FCSTD DOCUMENT  (FreeCAD 0.19R24267 +99 (Git))
Label: OTP20_PCB_Assembly
License: Creative Commons Attribution-NonCommercial-ShareAlike
LicenseURL: http://creativecommons.org/licenses/by-nc-sa/4.0/
objects: App::Link×6, App::DocumentObjectGroup×2, PartDesign::CoordinateSystem×1, App::FeaturePython×1, App::Part×1
note: 1 computed .brp shape members not serialized (recipe doc carries the construction recipe); baked Part::Feature solids carry a one-line shape summary decoded from their .brp
EXTERNAL_REF file=PCB_Outline.FCStd obj=LCS_0
EXTERNAL_REF file=PCB_Outline.FCStd obj=PCB_Board
EXTERNAL_REF file=../20_COTS/Lightpipe_Mentor_1296-2012.FCStd obj=LCS_0
EXTERNAL_REF file=../20_COTS/Lightpipe_Mentor_1296-2012.FCStd obj=Lightpipe
EXTERNAL_REF file=../20_COTS/USB_A_Connector_Wuerth.FCStd obj=USB_A_Connector
EXTERNAL_REF file=../20_COTS/USB_A_Connector_Wuerth.FCStd obj=LCS_0
EXTERNAL_REF file=../20_COTS/USB_C_Connector_Wuerth.FCStd obj=USB_C_Connector
EXTERNAL_REF file=Main_PCB.FCStd obj=LCS_0
EXTERNAL_REF file=Main_PCB.FCStd obj=Main_PCB

FEATURE [App::DocumentObjectGroup] Parts
FEATURE [PartDesign::CoordinateSystem] LCS_Origin  label="LCS_PCB"
  AttacherType = Attacher::AttachEngine3D
  MapMode = 2
  Support = -> [X_Axis]
FEATURE [App::DocumentObjectGroup] Constraints
FEATURE [App::FeaturePython] Variables  # WARN: FeaturePython — macro-defined, semantics opaque (R4)
  Connector_Inserted = 20
FEATURE [App::Link] PCB_Outline_PCB_Board
  AssemblyType = Asm4EE
  AttachedBy = #LCS_0
  AttachedTo = Parent Assembly#LCS_Origin
  LinkedObject = -> <external PCB_Outline.FCStd>#PCB_Board
  expr: Placement = LCS_Origin.Placement * AttachmentOffset * PCB_Outline#LCS_0.Placement ^ -1
FEATURE [App::Link] Lightpipe_Mentor_1296_2012_Lightpipe
  AssemblyType = Asm4EE
  AttachedBy = #LCS_0
  AttachedTo = PCB_Outline_PCB_Board#LCS_0
  AttachmentOffset = pos=(88,0,2.54) rot=(0,0,1;4.71239rad)
  LinkPlacement = pos=(88,0,2.54) rot=(0,0,1;4.71239rad)
  LinkedObject = -> <external ../20_COTS/Lightpipe_Mentor_1296-2012.FCStd>#Lightpipe
  Placement = pos=(88,0,2.54) rot=(0,0,1;4.71239rad)
  expr: Placement = PCB_Outline_PCB_Board.Placement * PCB_Outline#LCS_0.Placement * AttachmentOffset * Lightpipe_Mentor_1296_2012#LCS_0.Placement ^ -1
FEATURE [App::Link] USB_A_Connector_Wuerth_USB_A_Connector
  AssemblyType = Asm4EE
  AttachedBy = #LCS_0
  AttachedTo = Parent Assembly#LCS_Origin
  AttachmentOffset = pos=(42,-4,4.05) rot=(0,0,1;3.14159rad)
  LinkPlacement = pos=(42,-24,4.05) rot=(0,0,1;3.14159rad)
  LinkedObject = -> <external ../20_COTS/USB_A_Connector_Wuerth.FCStd>#USB_A_Connector
  Placement = pos=(42,-24,4.05) rot=(0,0,1;3.14159rad)
  expr: .Placement.Base.y = -4mm - Variables.Connector_Inserted * 1mm
FEATURE [App::Link] USB_A_Connector_Wuerth_USB_A_Connector001
  AssemblyType = Asm4EE
  AttachedBy = #LCS_0
  AttachedTo = USB_A_Connector_Wuerth_USB_A_Connector#LCS_0
  AttachmentOffset = pos=(18,0,0) rot=(0,0,1;0rad)
  LinkPlacement = pos=(24,-24,4.05) rot=(0,0,1;3.14159rad)
  LinkedObject = -> <external ../20_COTS/USB_A_Connector_Wuerth.FCStd>#USB_A_Connector
  Placement = pos=(24,-24,4.05) rot=(0,0,1;3.14159rad)
  expr: Placement = USB_A_Connector_Wuerth_USB_A_Connector.Placement * USB_A_Connector_Wuerth#LCS_0.Placement * AttachmentOffset * USB_A_Connector_Wuerth#LCS_0.Placement ^ -1
FEATURE [App::Link] USB_C_Connector_Wuerth_USB_C_Connector
  AssemblyType = Asm4EE
  AttachedBy = #LCS_USB_C_CenterCase
  AttachedTo = PCB_Outline_PCB_Board#LCS_0
  AttachmentOffset = pos=(7,-1,1.5) rot=(1,0,0;1.5708rad)
  LinkPlacement = pos=(7,-17,1.5) rot=(0,-0.707107,-0.707107;3.14159rad)
  LinkedObject = -> <external ../20_COTS/USB_C_Connector_Wuerth.FCStd>#USB_C_Connector
  Placement = pos=(7,-17,1.5) rot=(0,-0.707107,-0.707107;3.14159rad)
  expr: .Placement.Base.y = 3mm - Variables.Connector_Inserted * 1mm
FEATURE [App::Link] Main_PCB_Main_PCB
  AssemblyType = Asm4EE
  AttachedBy = #LCS_0
  AttachedTo = PCB_Outline_PCB_Board#LCS_0
  LinkedObject = -> <external Main_PCB.FCStd>#Main_PCB
  expr: Placement = PCB_Outline_PCB_Board.Placement * PCB_Outline#LCS_0.Placement * AttachmentOffset * Main_PCB#LCS_0.Placement ^ -1
FEATURE [App::Part] Model
  Configuration = 0
  Group = -> [LCS_Origin,Constraints,Variables,PCB_Outline_PCB_Board,Lightpipe_Mentor_1296_2012_Lightpipe,USB_A_Connector_Wuerth_USB_A_Connector,USB_A_Connector_Wuerth_USB_A_Connector001,USB_C_Connector_Wuerth_USB_C_Connector,Main_PCB_Main_PCB]
  Origin = -> Origin
  Type = Assembly4 Model

RESOLVED EXTERNAL PARTS (link-assembly join: the EXTERNAL_REF files above that resolve inside this repo's crawl, each included once):
---- part ../20_COTS/Lightpipe_Mentor_1296-2012.FCStd = doc fcstd_3caebb058678 ----
FCSTD DOCUMENT  (FreeCAD 0.19R24267 +99 (Git))
Label: Lightpipe_Mentor_1296-2012
License: Creative Commons Attribution-NonCommercial-ShareAlike
LicenseURL: http://creativecommons.org/licenses/by-nc-sa/4.0/
objects: Sketcher::SketchObject×7, PartDesign::Pad×5, PartDesign::LinearPattern×2, PartDesign::Revolution×1, PartDesign::Pocket×1, PartDesign::Chamfer×1, PartDesign::Body×1, PartDesign::CoordinateSystem×1, App::Part×1
note: 27 computed .brp shape members not serialized (recipe doc carries the construction recipe); baked Part::Feature solids carry a one-line shape summary decoded from their .brp

FEATURE [Sketcher::SketchObject] Sketch
  FullyConstrained = true
  MapMode = 5
  Placement = pos=(0,0,0) rot=(1,0,0;1.5708rad)
  Support = -> [XZ_Plane]
  sketch-geometry (5):
    g0: LineSegment StartX=0 StartY=0 StartZ=0 EndX=0 EndY=0.975 EndZ=0
    g1: LineSegment StartX=0 StartY=0.975 StartZ=0 EndX=2.5 EndY=0.975 EndZ=0
    g2: LineSegment StartX=2.5 StartY=0.975 StartZ=0 EndX=2.5 EndY=0.775 EndZ=0
    g3: ArcOfCircle CenterX=1.64896 CenterY=0 CenterZ=0 NormalX=0 NormalY=0 NormalZ=1 AngleXU=0 Radius=1.15104 StartAngle=0 EndAngle=0.738667
    g4: LineSegment StartX=2.8 StartY=0 StartZ=0 EndX=0 EndY=0 EndZ=0
  constraints (15):
    c: Coincident(g-1,g0)
    c: PointOnObject(g0,g-2)
    c: Coincident(g0,g1)
    c: Horizontal(g1)
    c: Coincident(g1,g2)
    c: PointOnObject(g3,g-1)
    c: Coincident(g3,g4)
    c: Coincident(g4,g0)
    c: Coincident(g3,g2)
    c: PointOnObject(g3,g-1)
    c: Distance(g0) = 0.975
    c: Vertical(g2)
    c: Distance(g4) = 2.8
    c: Distance(g1) = 2.5
    c: Distance(g2) = 0.2
FEATURE [Sketcher::SketchObject] Sketch001
  FullyConstrained = true
  MapMode = 5
  Placement = pos=(0,0,0) rot=(0.57735,0.57735,0.57735;2.0944rad)
  Support = -> [YZ_Plane]
  sketch-geometry (4):
    g0: LineSegment StartX=-0.975 StartY=3.515 StartZ=0 EndX=0.975 EndY=3.515 EndZ=0
    g1: LineSegment StartX=0.975 StartY=3.515 StartZ=0 EndX=0.975 EndY=-0.975 EndZ=0
    g2: LineSegment StartX=0.975 StartY=-0.975 StartZ=0 EndX=-0.975 EndY=-0.975 EndZ=0
    g3: LineSegment StartX=-0.975 StartY=-0.975 StartZ=0 EndX=-0.975 EndY=3.515 EndZ=0
  constraints (11):
    c: Coincident(g0,g1)
    c: Coincident(g1,g2)
    c: Coincident(g2,g3)
    c: Coincident(g3,g0)
    c: Horizontal(g0)
    c: Vertical(g1)
    c: Vertical(g3)
    c: Symmetric(g2,g1,g-2)
    c: Distance(g0) = 1.95
    c: Distance(g1) = 4.49
    c: Distance(g-1,g2) = 0.975
FEATURE [PartDesign::Pad] Pad
  Direction = (1,1,1)
  Length = 0.5
  Length2 = 100
  Placement = pos=(0,0,0) rot=(0.57735,0.57735,0.57735;2.0944rad)
  Profile = -> Sketch001
  Refine = true
  Reversed = true
  Type = 0
FEATURE [PartDesign::Revolution] Revolution
  Angle = 360
  Axis = (1,0,0)
  Base = (0,0,0)
  BaseFeature = -> Pad
  Placement = pos=(0,0,0) rot=(0.57735,0.57735,0.57735;2.0944rad)
  Profile = -> Sketch
  ReferenceAxis = -> X_Axis
  Refine = true
  Reversed = true
FEATURE [PartDesign::LinearPattern] LinearPattern
  BaseFeature = -> Revolution
  Direction = -> Z_Axis
  Length = 2.54
  Occurrences = 2
  Originals = -> [Revolution]
  Placement = pos=(0,0,0) rot=(0.57735,0.57735,0.57735;2.0944rad)
  Refine = true
FEATURE [Sketcher::SketchObject] Sketch002
  FullyConstrained = true
  MapMode = 5
  Placement = pos=(0,0,0) rot=(1,0,0;1.5708rad)
  Support = -> [XZ_Plane]
  sketch-geometry (6):
    g0: LineSegment StartX=-0.5 StartY=3.515 StartZ=0 EndX=-4.485 EndY=3.515 EndZ=0
    g1: ArcOfCircle CenterX=-4.485 CenterY=0 CenterZ=0 NormalX=0 NormalY=0 NormalZ=1 AngleXU=0 Radius=3.515 StartAngle=1.5708 EndAngle=3.14159
    g2: LineSegment StartX=-8 StartY=4e-16 StartZ=0 EndX=-6.05 EndY=4e-16 EndZ=0
    g3: LineSegment StartX=-4.485 StartY=1.565 StartZ=0 EndX=-0.5 EndY=1.565 EndZ=0
    g4: LineSegment StartX=-0.5 StartY=1.565 StartZ=0 EndX=-0.5 EndY=3.515 EndZ=0
    g5: ArcOfCircle CenterX=-4.485 CenterY=0 CenterZ=0 NormalX=0 NormalY=0 NormalZ=1 AngleXU=0 Radius=1.565 StartAngle=1.5708 EndAngle=3.14159
  constraints (17):
    c: Horizontal(g0)
    c: Tangent(g0,g1) = -1.5708
    c: Angle(g1) = 1.5708
    c: Horizontal(g2)
    c: Coincident(g3,g4)
    c: Coincident(g4,g0)
    c: Coincident(g2,g1)
    c: Horizontal(g3)
    c: Vertical(g4)
    c: Coincident(g5,g1)
    c: Coincident(g5,g2)
    c: Tangent(g5,g3) = 1.5708
    c: PointOnObject(g1,g-1)
    c: Distance(g2) = 1.95
    c: DistanceY(g-1,g0) = 3.515
    c: DistanceX(g-2,g3) = -0.5
    c: DistanceX(g-2,g1) = -8
FEATURE [PartDesign::Pad] Pad001
  BaseFeature = -> LinearPattern
  Direction = (1,1,1)
  Length = 1.95
  Length2 = 100
  Midplane = true
  Placement = pos=(0,0,0) rot=(0.57735,0.57735,0.57735;2.0944rad)
  Profile = -> Sketch002
  Refine = true
  Type = 0
FEATURE [Sketcher::SketchObject] Sketch003
  FullyConstrained = true
  MapMode = 5
  Placement = pos=(0,0,0) rot=(1,0,0;1.5708rad)
  Support = -> [XZ_Plane]
  sketch-geometry (4):
    g0: LineSegment StartX=-0.5 StartY=0.975 StartZ=0 EndX=-3.55 EndY=0.975 EndZ=0
    g1: LineSegment StartX=-5.5 StartY=-0.975 StartZ=0 EndX=-0.5 EndY=-0.975 EndZ=0
    g2: LineSegment StartX=-0.5 StartY=-0.975 StartZ=0 EndX=-0.5 EndY=0.975 EndZ=0
    g3: LineSegment StartX=-3.55 StartY=0.975 StartZ=0 EndX=-5.5 EndY=-0.975 EndZ=0
  constraints (11):
    c: Horizontal(g0)
    c: Coincident(g1,g2)
    c: Coincident(g2,g0)
    c: Horizontal(g1)
    c: DistanceX(g-2,g1) = -0.5
    c: Distance(g2) = 1.95
    c: Symmetric(g1,g0,g-1)
    c: Coincident(g3,g0)
    c: Coincident(g3,g1)
    c: Angle(g1,g3) = 0.785398
    c: Distance(g1) = 5
FEATURE [PartDesign::Pad] Pad002
  BaseFeature = -> Pad001
  Direction = (1,1,1)
  Length = 1.95
  Length2 = 100
  Midplane = true
  Placement = pos=(0,0,0) rot=(0.57735,0.57735,0.57735;2.0944rad)
  Profile = -> Sketch003
  Refine = true
  Type = 0
FEATURE [Sketcher::SketchObject] Sketch004
  FullyConstrained = true
  MapMode = 5
  Placement = pos=(0,0,0) rot=(1,0,0;1.5708rad)
  Support = -> [XZ_Plane]
  sketch-geometry (6):
    g0: LineSegment StartX=0 StartY=-2.54 StartZ=0 EndX=-9.05 EndY=-2.54 EndZ=0
    g1: LineSegment StartX=-9.05 StartY=-2.54 StartZ=0 EndX=-9.05 EndY=0.5 EndZ=0
    g2: LineSegment StartX=-9.05 StartY=0.5 StartZ=0 EndX=-3.05 EndY=0.5 EndZ=0
    g3: LineSegment StartX=-3.05 StartY=0.5 StartZ=0 EndX=-3.05 EndY=-1.14 EndZ=0
    g4: LineSegment StartX=-3.05 StartY=-1.14 StartZ=0 EndX=0 EndY=-1.14 EndZ=0
    g5: LineSegment StartX=0 StartY=-1.14 StartZ=0 EndX=0 EndY=-2.54 EndZ=0
  constraints (18):
    c: PointOnObject(g0,g-2)
    c: Horizontal(g0)
    c: Coincident(g0,g1)
    c: Coincident(g1,g2)
    c: Horizontal(g2)
    c: Coincident(g2,g3)
    c: Coincident(g3,g4)
    c: PointOnObject(g4,g-2)
    c: Horizontal(g4)
    c: Coincident(g4,g5)
    c: Coincident(g5,g0)
    c: Vertical(g3)
    c: Vertical(g1)
    c: Distance(g-1,g1) = 9.05
    c: DistanceY(g-1,g0) = -2.54
    c: Distance(g5) = 1.4
    c: Distance(g-1,g2) = 0.5
    c: Distance(g2) = 6
FEATURE [PartDesign::Pad] Pad003
  BaseFeature = -> Pad002
  Direction = (1,1,1)
  Length = 3.16
  Length2 = 100
  Midplane = true
  Placement = pos=(0,0,0) rot=(0.57735,0.57735,0.57735;2.0944rad)
  Profile = -> Sketch004
  Refine = true
  Type = 0
FEATURE [Sketcher::SketchObject] Sketch005
  FullyConstrained = true
  MapMode = 5
  Placement = pos=(0,-1.1e-15,-2.54) rot=(0.707107,0.707107,0;3.14159rad)
  Support = -> [Pad003]
  sketch-geometry (8):
    g0: LineSegment StartX=-0.975 StartY=0 StartZ=0 EndX=0.975 EndY=0 EndZ=0
    g1: LineSegment StartX=0.975 StartY=0 StartZ=0 EndX=0.975 EndY=-4.5 EndZ=0
    g2: LineSegment StartX=0.975 StartY=-4.5 StartZ=0 EndX=-0.975 EndY=-4.5 EndZ=0
    g3: LineSegment StartX=-0.975 StartY=-4.5 StartZ=0 EndX=-0.975 EndY=0 EndZ=0
    g4: LineSegment StartX=-0.975 StartY=-5 StartZ=0 EndX=0.975 EndY=-5 EndZ=0
    g5: LineSegment StartX=0.975 StartY=-5 StartZ=0 EndX=0.975 EndY=-9.05 EndZ=0
    g6: LineSegment StartX=0.975 StartY=-9.05 StartZ=0 EndX=-0.975 EndY=-9.05 EndZ=0
    g7: LineSegment StartX=-0.975 StartY=-9.05 StartZ=0 EndX=-0.975 EndY=-5 EndZ=0
  constraints (23):
    c: Coincident(g0,g1)
    c: Coincident(g1,g2)
    c: Coincident(g2,g3)
    c: Coincident(g3,g0)
    c: Horizontal(g0)
    c: Horizontal(g2)
    c: Vertical(g1)
    c: Vertical(g3)
    c: Coincident(g4,g5)
    c: Coincident(g5,g6)
    c: Coincident(g6,g7)
    c: Coincident(g7,g4)
    c: Horizontal(g6)
    c: Vertical(g5)
    c: Vertical(g7)
    c: Distance(g6) = 1.95
    c: Vertical(g4,g2)
    c: Vertical(g4,g1)
    c: Symmetric(g4,g4,g-2)
    c: Distance(g-1,g6) = 9.05
    c: Distance(g4,g2) = 0.5
    c: PointOnObject(g-1,g0)
    c: Distance(g-1,g2) = 4.5
FEATURE [PartDesign::Pocket] Pocket
  BaseFeature = -> Pad003
  Length = 1
  Length2 = 100
  Placement = pos=(0,0,0) rot=(0.57735,0.57735,0.57735;2.0944rad)
  Profile = -> Sketch005
  Refine = true
  Type = 0
FEATURE [Sketcher::SketchObject] Sketch006
  FullyConstrained = true
  MapMode = 5
  Support = -> [XY_Plane]
  sketch-geometry (1):
    g0: Circle CenterX=-1.4 CenterY=0 CenterZ=0 NormalX=0 NormalY=0 NormalZ=1 AngleXU=0 Radius=0.6
  constraints (3):
    c: PointOnObject(g0,g-1)
    c: Diameter(g0) = 1.2
    c: DistanceX(g-2,g0) = -1.4
FEATURE [PartDesign::Pad] Pad004
  BaseFeature = -> Pocket
  Direction = (1,1,1)
  Length = 4.64
  Length2 = 100
  Placement = pos=(0,0,0) rot=(0.57735,0.57735,0.57735;2.0944rad)
  Profile = -> Sketch006
  Refine = true
  Reversed = true
  Type = 0
FEATURE [PartDesign::LinearPattern] LinearPattern001
  BaseFeature = -> Pad004
  Direction = -> X_Axis
  Length = 6.6
  Occurrences = 2
  Originals = -> [Pad004]
  Placement = pos=(0,0,0) rot=(0.57735,0.57735,0.57735;2.0944rad)
  Refine = true
  Reversed = true
FEATURE [PartDesign::Chamfer] Chamfer
  Angle = 20
  Base = -> LinearPattern001 [Edge110,Edge108]
  BaseFeature = -> LinearPattern001
  ChamferType = 2
  FlipDirection = false
  Placement = pos=(0,0,0) rot=(0.57735,0.57735,0.57735;2.0944rad)
  Refine = true
  Size = 0.8
  Size2 = 1
  SupportTransform = false
FEATURE [PartDesign::Body] Body
  Group = -> [Sketch,Sketch001,Pad,Revolution,LinearPattern,Sketch002,Pad001,Sketch003,Pad002,Sketch004,Pad003,Sketch005,Pocket,Sketch006,Pad004,LinearPattern001,Chamfer]
  Origin = -> Origin
  Tip = -> Chamfer
FEATURE [PartDesign::CoordinateSystem] LCS_0
  AttacherType = Attacher::AttachEngine3D
  MapMode = 2
  Support = -> [X_Axis001]
FEATURE [App::Part] Lightpipe
  Group = -> [LCS_0,Body]
  Origin = -> Origin001
---- part ../20_COTS/USB_C_Connector_Wuerth.FCStd = doc fcstd_f73dced2f54f ----
FCSTD DOCUMENT  (FreeCAD 0.19R24267 +99 (Git))
Label: USB_C_Connector_Wuerth
License: Creative Commons Attribution-NonCommercial-ShareAlike
LicenseURL: http://creativecommons.org/licenses/by-nc-sa/4.0/
objects: Part::Feature×33, App::Part×5, Sketcher::SketchObject×5, PartDesign::Plane×3, PartDesign::Pad×3, PartDesign::Fillet×2, PartDesign::Pocket×2, PartDesign::CoordinateSystem×2, PartDesign::LinearPattern×1, PartDesign::Body×1
note: 59 computed .brp shape members not serialized (recipe doc carries the construction recipe); baked Part::Feature solids carry a one-line shape summary decoded from their .brp

FEATURE [Part::Feature] Part__Feature  label="632712000112_Shelding"
  shape: bbox 8.543 x 3.737 x 11.66 mm, 85 faces (baked)
FEATURE [Part::Feature] Part__Feature001  label="632712000112_Housing1"
  Placement = pos=(1e-15,-3e-15,-0.02) rot=(0,0,1;0rad)
  shape: bbox 8.291 x 3.729 x 11.09 mm, 630 faces (baked)
FEATURE [Part::Feature] Part__Feature002  label="632712000112_Housing2"
  shape: bbox 6.83 x 0.9 x 4.9 mm, 171 faces (baked)
FEATURE [Part::Feature] Part__Feature003  label="632712000112_Pin"
  Placement = pos=(-2.75,-0.26,0) rot=(0,0,1;3.14159rad)
  shape: bbox 0.2209 x 0.7139 x 9.499 mm, 32 faces (baked)
FEATURE [Part::Feature] Part__Feature004  label="632712000112_Pin001"
  Placement = pos=(-2.25,-0.26,-1e-15) rot=(0,0,1;3.14159rad)
  shape: bbox 0.2209 x 0.7139 x 9.499 mm, 32 faces (baked)
FEATURE [Part::Feature] Part__Feature005  label="632712000112_Pin002"
  Placement = pos=(-1.75,-0.26,-1e-15) rot=(0,0,1;3.14159rad)
  shape: bbox 0.2209 x 0.7139 x 9.499 mm, 32 faces (baked)
FEATURE [Part::Feature] Part__Feature006  label="632712000112_Pin003"
  Placement = pos=(-1.25,-0.26,-1e-15) rot=(0,0,1;3.14159rad)
  shape: bbox 0.2209 x 0.7139 x 9.499 mm, 32 faces (baked)
FEATURE [Part::Feature] Part__Feature007  label="632712000112_Pin004"
  Placement = pos=(-0.75,-0.26,-2e-15) rot=(0,0,1;3.14159rad)
  shape: bbox 0.2209 x 0.7139 x 9.499 mm, 32 faces (baked)
FEATURE [Part::Feature] Part__Feature008  label="632712000112_Pin005"
  Placement = pos=(-0.25,-0.26,-2e-15) rot=(0,0,1;3.14159rad)
  shape: bbox 0.2209 x 0.7139 x 9.499 mm, 32 faces (baked)
FEATURE [Part::Feature] Part__Feature009  label="632712000112_Pin006"
  Placement = pos=(0.25,-0.26,-2e-15) rot=(0,0,1;3.14159rad)
  shape: bbox 0.2209 x 0.7139 x 9.499 mm, 32 faces (baked)
FEATURE [Part::Feature] Part__Feature010  label="632712000112_Pin007"
  Placement = pos=(0.75,-0.26,-2e-15) rot=(0,0,1;3.14159rad)
  shape: bbox 0.2209 x 0.7139 x 9.499 mm, 32 faces (baked)
FEATURE [Part::Feature] Part__Feature011  label="632712000112_Pin008"
  Placement = pos=(1.25,-0.26,-3e-15) rot=(0,0,1;3.14159rad)
  shape: bbox 0.2209 x 0.7139 x 9.499 mm, 32 faces (baked)
FEATURE [Part::Feature] Part__Feature012  label="632712000112_Pin009"
  Placement = pos=(1.75,-0.26,-3e-15) rot=(0,0,1;3.14159rad)
  shape: bbox 0.2209 x 0.7139 x 9.499 mm, 32 faces (baked)
FEATURE [Part::Feature] Part__Feature013  label="632712000112_Pin010"
  Placement = pos=(2.25,-0.26,-3e-15) rot=(0,0,1;3.14159rad)
  shape: bbox 0.2209 x 0.7139 x 9.499 mm, 32 faces (baked)
FEATURE [Part::Feature] Part__Feature014  label="632712000112_Pin011"
  Placement = pos=(2.75,-0.26,-4e-15) rot=(0,0,1;3.14159rad)
  shape: bbox 0.2209 x 0.7139 x 9.499 mm, 32 faces (baked)
FEATURE [App::Part] SE_Shelding_Pin  label="SE Shelding Pin"
  Group = -> [Part__Feature002,Part__Feature003,Part__Feature004,Part__Feature005,Part__Feature006,Part__Feature007,Part__Feature008,Part__Feature009,Part__Feature010,Part__Feature011,Part__Feature012,Part__Feature013,Part__Feature014]
  Origin = -> Origin
  Placement = pos=(-8.37e-14,-0.2,-7.98) rot=(0,0,1;0rad)
FEATURE [Part::Feature] Part__Feature015  label="632712000112_Shelding2.asm"
  Placement = pos=(1e-15,-1.03,-5.2) rot=(0,0,1;3.14159rad)
  shape: bbox 6.32 x 1.17 x 9.76 mm, 166 faces (baked)
FEATURE [Part::Feature] Part__Feature016  label="632712000112_Shelding3.asm"
  Placement = pos=(0,-0.2,-7.2289) rot=(0,0,1;0rad)
  shape: bbox 7.6 x 1.69 x 9.87 mm, 88 faces (baked)
FEATURE [Part::Feature] Part__Feature017  label="632712000112_Shelding2.asm001"
  Placement = pos=(0,1.03,-5.2) rot=(0,0,1;0rad)
  shape: bbox 6.32 x 1.17 x 9.76 mm, 166 faces (baked)
FEATURE [Part::Feature] Part__Feature018  label="632712000112_Housing003"
  shape: bbox 6.83 x 0.9 x 4.9 mm, 171 faces (baked)
FEATURE [Part::Feature] Part__Feature019  label="632712000112_Pin012"
  Placement = pos=(-2.75,-0.26,0) rot=(0,0,1;3.14159rad)
  shape: bbox 0.2209 x 0.7139 x 9.499 mm, 32 faces (baked)
FEATURE [Part::Feature] Part__Feature020  label="632712000112_Pin013"
  Placement = pos=(-2.25,-0.26,-1e-15) rot=(0,0,1;3.14159rad)
  shape: bbox 0.2209 x 0.7139 x 9.499 mm, 32 faces (baked)
FEATURE [Part::Feature] Part__Feature021  label="632712000112_Pin014"
  Placement = pos=(-1.75,-0.26,-1e-15) rot=(0,0,1;3.14159rad)
  shape: bbox 0.2209 x 0.7139 x 9.499 mm, 32 faces (baked)
FEATURE [Part::Feature] Part__Feature022  label="632712000112_Pin015"
  Placement = pos=(-1.25,-0.26,-1e-15) rot=(0,0,1;3.14159rad)
  shape: bbox 0.2209 x 0.7139 x 9.499 mm, 32 faces (baked)
FEATURE [Part::Feature] Part__Feature023  label="632712000112_Pin016"
  Placement = pos=(-0.75,-0.26,-2e-15) rot=(0,0,1;3.14159rad)
  shape: bbox 0.2209 x 0.7139 x 9.499 mm, 32 faces (baked)
FEATURE [Part::Feature] Part__Feature024  label="632712000112_Pin017"
  Placement = pos=(-0.25,-0.26,-2e-15) rot=(0,0,1;3.14159rad)
  shape: bbox 0.2209 x 0.7139 x 9.499 mm, 32 faces (baked)
FEATURE [Part::Feature] Part__Feature025  label="632712000112_Pin018"
  Placement = pos=(0.25,-0.26,-2e-15) rot=(0,0,1;3.14159rad)
  shape: bbox 0.2209 x 0.7139 x 9.499 mm, 32 faces (baked)
FEATURE [Part::Feature] Part__Feature026  label="632712000112_Pin019"
  Placement = pos=(0.75,-0.26,-2e-15) rot=(0,0,1;3.14159rad)
  shape: bbox 0.2209 x 0.7139 x 9.499 mm, 32 faces (baked)
FEATURE [Part::Feature] Part__Feature027  label="632712000112_Pin020"
  Placement = pos=(1.25,-0.26,-3e-15) rot=(0,0,1;3.14159rad)
  shape: bbox 0.2209 x 0.7139 x 9.499 mm, 32 faces (baked)
FEATURE [Part::Feature] Part__Feature028  label="632712000112_Pin021"
  Placement = pos=(1.75,-0.26,-3e-15) rot=(0,0,1;3.14159rad)
  shape: bbox 0.2209 x 0.7139 x 9.499 mm, 32 faces (baked)
FEATURE [Part::Feature] Part__Feature029  label="632712000112_Pin022"
  Placement = pos=(2.25,-0.26,-3e-15) rot=(0,0,1;3.14159rad)
  shape: bbox 0.2209 x 0.7139 x 9.499 mm, 32 faces (baked)
FEATURE [Part::Feature] Part__Feature030  label="632712000112_Pin023"
  Placement = pos=(2.75,-0.26,-4e-15) rot=(0,0,1;3.14159rad)
  shape: bbox 0.2209 x 0.7139 x 9.499 mm, 32 faces (baked)
FEATURE [App::Part] SE_Shelding_Pin001  label="SE Shelding Pin001"
  Group = -> [Part__Feature018,Part__Feature019,Part__Feature020,Part__Feature021,Part__Feature022,Part__Feature023,Part__Feature024,Part__Feature025,Part__Feature026,Part__Feature027,Part__Feature028,Part__Feature029,Part__Feature030]
  Origin = -> Origin001
  Placement = pos=(-8.04e-14,0.2,-7.98) rot=(0,0,1;3.14159rad)
FEATURE [Part::Feature] Part__Feature031  label="632712000112_Mylar"
  Placement = pos=(0,-0.98,-2.44) rot=(0,0.707107,-0.707107;3.14159rad)
  shape: bbox 5.95 x 0.05 x 1.6 mm, 6 faces (baked)
FEATURE [Part::Feature] Part__Feature032  label="632712000112_Mylar001"
  Placement = pos=(0,0.98,-2.49) rot=(0,0.707107,0.707107;3.14159rad)
  shape: bbox 5.95 x 0.05 x 1.6 mm, 6 faces (baked)
FEATURE [App::Part] _32712000112  label="Plug"
  Group = -> [Part__Feature,Part__Feature001,SE_Shelding_Pin,Part__Feature015,Part__Feature016,Part__Feature017,SE_Shelding_Pin001,Part__Feature031,Part__Feature032]
  Origin = -> Origin002
FEATURE [PartDesign::Plane] DatumPlane
  AttachmentOffset = pos=(0,0,-6.65) rot=(0,0,1;0rad)
  Length = 60
  MapMode = 5
  Placement = pos=(0,0,-6.65) rot=(0,0,1;0rad)
  ResizeMode = 0
  Support = -> [XY_Plane004]
  Width = 60
FEATURE [Sketcher::SketchObject] Sketch
  FullyConstrained = true
  MapMode = 5
  Placement = pos=(0,0,-6.65) rot=(0,0,1;0rad)
  Support = -> [DatumPlane]
  sketch-geometry (6):
    g0: ArcOfCircle CenterX=-2.75 CenterY=0 CenterZ=0 NormalX=0 NormalY=0 NormalZ=1 AngleXU=0 Radius=3.35 StartAngle=1.5708 EndAngle=4.71239
    g1: ArcOfCircle CenterX=2.75 CenterY=0 CenterZ=0 NormalX=0 NormalY=0 NormalZ=1 AngleXU=0 Radius=3.35 StartAngle=4.71239 EndAngle=7.85398
    g2: LineSegment StartX=-2.75 StartY=-3.35 StartZ=0 EndX=2.75 EndY=-3.35 EndZ=0
    g3: LineSegment StartX=-2.75 StartY=3.35 StartZ=0 EndX=2.75 EndY=3.35 EndZ=0
    g4: GeomPoint X=-6.1 Y=0 Z=0
    g5: GeomPoint X=6.1 Y=0 Z=0
  constraints (13):
    c: Tangent(g0,g3) = 1.5708
    c: Tangent(g0,g2) = -1.5708
    c: Tangent(g2,g1) = -1.5708
    c: Tangent(g3,g1) = 1.5708
    c: Horizontal(g2)
    c: PointOnObject(g0,g-1)
    c: DistanceY(g0,g0) = 6.7
    c: PointOnObject(g4,g0)
    c: PointOnObject(g5,g1)
    c: PointOnObject(g5,g-1)
    c: PointOnObject(g4,g-1)
    c: DistanceX(g4,g5) = 12.2
    c: Symmetric(g0,g1,g-2)
FEATURE [PartDesign::Pad] Pad
  Direction = (1,1,1)
  Length = 19.45
  Length2 = 100
  Placement = pos=(0,0,-6.65) rot=(0,0,1;0rad)
  Profile = -> Sketch
  Refine = true
  Reversed = true
  Type = 0
FEATURE [PartDesign::Fillet] Fillet
  Base = -> Pad [Edge10,Edge9]
  BaseFeature = -> Pad
  Placement = pos=(0,0,-6.65) rot=(0,0,1;0rad)
  Radius = 0.5
  Refine = true
  SupportTransform = false
FEATURE [PartDesign::Plane] DatumPlane001
  AttachmentOffset = pos=(0,0,-19.45) rot=(0,0,1;0rad)
  Length = 60
  MapMode = 5
  Placement = pos=(0,0,-26.1) rot=(0,0,1;0rad)
  ResizeMode = 0
  Support = -> [DatumPlane]
  Width = 60
FEATURE [Sketcher::SketchObject] Sketch001
  AttachmentOffset = pos=(0,0,2) rot=(0,0,1;0rad)
  FullyConstrained = true
  MapMode = 5
  Placement = pos=(0,0,-24.1) rot=(0,0,1;0rad)
  Support = -> [DatumPlane001]
  sketch-geometry (1):
    g0: Circle CenterX=0 CenterY=0 CenterZ=0 NormalX=0 NormalY=0 NormalZ=1 AngleXU=0 Radius=3.34
  constraints (2):
    c: Coincident(g0,g-1)
    c: Radius(g0) = 3.34
FEATURE [PartDesign::Plane] DatumPlane002
  AttachmentOffset = pos=(0,0,-30.37) rot=(0,0,1;0rad)
  Length = 60
  MapMode = 5
  Placement = pos=(0,0,-37.02) rot=(0,0,1;0rad)
  ResizeMode = 0
  Support = -> [DatumPlane]
  Width = 60
FEATURE [PartDesign::Pad] Pad001
  BaseFeature = -> Fillet
  Direction = (1,1,1)
  Length = 10
  Length2 = 100
  Placement = pos=(0,0,-6.65) rot=(0,0,1;0rad)
  Profile = -> Sketch001
  Refine = true
  Type = 3
  UpToFace = -> DatumPlane002
FEATURE [Sketcher::SketchObject] Sketch002
  FullyConstrained = true
  MapMode = 5
  Placement = pos=(0,0,-37.02) rot=(0,0,1;0rad)
  Support = -> [DatumPlane002]
  sketch-geometry (1):
    g0: Circle CenterX=0 CenterY=0 CenterZ=0 NormalX=0 NormalY=0 NormalZ=1 AngleXU=0 Radius=2.25
  constraints (2):
    c: Coincident(g0,g-1)
    c: Radius(g0) = 2.25
FEATURE [PartDesign::Pad] Pad002
  BaseFeature = -> Pad001
  Direction = (1,1,1)
  Length = 20
  Length2 = 100
  Placement = pos=(0,0,-6.65) rot=(0,0,1;0rad)
  Profile = -> Sketch002
  Refine = true
  Reversed = true
  Type = 0
FEATURE [Sketcher::SketchObject] Sketch003
  FullyConstrained = true
  MapMode = 5
  Placement = pos=(0,-3.35,-6.65) rot=(1,0,0;1.5708rad)
  Support = -> [Pad002]
  sketch-geometry (2):
    g0: Circle CenterX=2 CenterY=-10 CenterZ=0 NormalX=0 NormalY=0 NormalZ=1 AngleXU=0 Radius=0.5
    g1: Circle CenterX=-2 CenterY=-10 CenterZ=0 NormalX=0 NormalY=0 NormalZ=1 AngleXU=0 Radius=0.5
  constraints (5):
    c: Symmetric(g1,g0,g-2)
    c: Equal(g1,g0)
    c: Radius(g0) = 0.5
    c: DistanceY(g-1,g0) = -10
    c: DistanceX(g1,g0) = 4
FEATURE [PartDesign::Pocket] Pocket
  BaseFeature = -> Pad002
  Length = 3
  Length2 = 100
  Placement = pos=(0,0,-6.65) rot=(0,0,1;0rad)
  Profile = -> Sketch003
  Refine = true
  Type = 0
FEATURE [PartDesign::Fillet] Fillet001
  Base = -> Pocket [Edge42]
  BaseFeature = -> Pocket
  Placement = pos=(0,0,-6.65) rot=(0,0,1;0rad)
  Radius = 0.5
  Refine = true
  SupportTransform = false
FEATURE [Sketcher::SketchObject] Sketch004
  AttachmentOffset = pos=(0,0,-2) rot=(0,0,1;0rad)
  FullyConstrained = true
  MapMode = 5
  Placement = pos=(0,0,-28.1) rot=(0,0,1;0rad)
  Support = -> [DatumPlane001]
  sketch-geometry (5):
    g0: Circle CenterX=3.88909 CenterY=3.88909 CenterZ=0 NormalX=0 NormalY=0 NormalZ=1 AngleXU=0 Radius=3.3
    g1: LineSegment StartX=0 StartY=0 StartZ=0 EndX=3.88909 EndY=3.88909 EndZ=0
    g2: Circle CenterX=3.88909 CenterY=-3.88909 CenterZ=0 NormalX=0 NormalY=0 NormalZ=1 AngleXU=0 Radius=3.3
    g3: Circle CenterX=-3.88909 CenterY=-3.88909 CenterZ=0 NormalX=0 NormalY=0 NormalZ=1 AngleXU=0 Radius=3.3
    g4: Circle CenterX=-3.88909 CenterY=3.88909 CenterZ=0 NormalX=0 NormalY=0 NormalZ=1 AngleXU=0 Radius=3.3
  constraints (11):
    c: Radius(g0) = 3.3
    c: Coincident(g1,g-1)
    c: Coincident(g1,g0)
    c: Angle(g-1,g1) = 0.785398
    c: Distance(g1) = 5.5
    c: Equal(g0,g4)
    c: Equal(g4,g3)
    c: Equal(g3,g2)
    c: Symmetric(g3,g0,g-1)
    c: Symmetric(g0,g2,g-1)
    c: Symmetric(g4,g0,g-2)
FEATURE [PartDesign::Pocket] Pocket001
  BaseFeature = -> Fillet001
  Length = 1
  Length2 = 100
  Placement = pos=(0,0,-6.65) rot=(0,0,1;0rad)
  Profile = -> Sketch004
  Refine = true
  Type = 0
FEATURE [PartDesign::LinearPattern] LinearPattern
  BaseFeature = -> Pocket001
  Direction = -> Z_Axis004
  Length = 6
  Occurrences = 4
  Originals = -> [Pocket001]
  Placement = pos=(0,0,-6.65) rot=(0,0,1;0rad)
  Refine = true
  Reversed = true
FEATURE [PartDesign::Body] Body
  Group = -> [DatumPlane,DatumPlane001,Sketch,Pad,Fillet,Sketch001,DatumPlane002,Pad001,Sketch002,Pad002,Sketch003,Pocket,Fillet001,Sketch004,Pocket001,LinearPattern]
  Origin = -> Origin004
  Tip = -> LinearPattern
FEATURE [App::Part] Part  label="Cable"
  Group = -> [Body]
  Origin = -> Origin003
FEATURE [PartDesign::CoordinateSystem] LCS_0
  AttacherType = Attacher::AttachEngine3D
  MapMode = 2
  Support = -> [X_Axis005]
FEATURE [PartDesign::CoordinateSystem] LCS_USB_C_CenterCase
  AttacherType = Attacher::AttachEngine3D
  AttachmentOffset = pos=(0,0,4) rot=(0,0,1;0rad)
  MapMode = 5
  Placement = pos=(0,0,-4) rot=(0,1,0;3.14159rad)
  Support = -> [XY_Plane005]
FEATURE [App::Part] USB_C_Connector
  Group = -> [LCS_0,Part,_32712000112,LCS_USB_C_CenterCase]
  Origin = -> Origin005
---- part PCB_Outline.FCStd = doc fcstd_bf06fc0350bf ----
FCSTD DOCUMENT  (FreeCAD 0.19R24267 +99 (Git))
Label: PCB_Outline
License: Creative Commons Attribution-NonCommercial-ShareAlike
LicenseURL: http://creativecommons.org/licenses/by-nc-sa/4.0/
objects: Sketcher::SketchObject×3, PartDesign::Fillet×3, PartDesign::CoordinateSystem×1, PartDesign::Pad×1, PartDesign::Pocket×1, PartDesign::Hole×1, PartDesign::Body×1, App::Part×1
note: 17 computed .brp shape members not serialized (recipe doc carries the construction recipe); baked Part::Feature solids carry a one-line shape summary decoded from their .brp

FEATURE [PartDesign::CoordinateSystem] LCS_0  label="LCS_PCB_CornerLeft"
  AttacherType = Attacher::AttachEngine3D
  MapMode = 2
  Support = -> [X_Axis]
FEATURE [Sketcher::SketchObject] Sketch
  FullyConstrained = true
  MapMode = 5
  Support = -> [XY_Plane001]
  sketch-geometry (6):
    g0: LineSegment StartX=0 StartY=0 StartZ=0 EndX=100 EndY=0 EndZ=0
    g1: LineSegment StartX=100 StartY=0 StartZ=0 EndX=100 EndY=25 EndZ=0
    g2: LineSegment StartX=100 StartY=25 StartZ=0 EndX=75 EndY=25 EndZ=0
    g3: LineSegment StartX=75 StartY=25 StartZ=0 EndX=75 EndY=55 EndZ=0
    g4: LineSegment StartX=75 StartY=55 StartZ=0 EndX=0 EndY=55 EndZ=0
    g5: LineSegment StartX=0 StartY=55 StartZ=0 EndX=0 EndY=0 EndZ=0
  constraints (17):
    c: Coincident(g-1,g0)
    c: PointOnObject(g0,g-1)
    c: Coincident(g0,g1)
    c: Vertical(g1)
    c: Coincident(g1,g2)
    c: Horizontal(g2)
    c: Coincident(g2,g3)
    c: Vertical(g3)
    c: Coincident(g3,g4)
    c: PointOnObject(g4,g-2)
    c: Horizontal(g4)
    c: Coincident(g4,g5)
    c: Coincident(g5,g0)
    c: Distance(g0) = 100
    c: Distance(g5) = 55
    c: Distance(g4) = 75
    c: Distance(g1) = 25
FEATURE [PartDesign::Pad] Pad
  Direction = (1,1,1)
  Length = 1.7
  Length2 = 100
  Profile = -> Sketch
  Refine = true
  Reversed = true
  Type = 0
FEATURE [Sketcher::SketchObject] Sketch001
  FullyConstrained = true
  MapMode = 5
  Support = -> [XY_Plane001]
  sketch-geometry (8):
    g0: LineSegment StartX=48.5 StartY=0 StartZ=0 EndX=86.4 EndY=0 EndZ=0
    g1: LineSegment StartX=86.4 StartY=0 StartZ=0 EndX=86.4 EndY=4 EndZ=0
    g2: LineSegment StartX=86.4 StartY=4 StartZ=0 EndX=48.5 EndY=4 EndZ=0
    g3: LineSegment StartX=48.5 StartY=4 StartZ=0 EndX=48.5 EndY=0 EndZ=0
    g4: LineSegment StartX=89.6 StartY=0 StartZ=0 EndX=100 EndY=0 EndZ=0
    g5: LineSegment StartX=100 StartY=0 StartZ=0 EndX=100 EndY=1 EndZ=0
    g6: LineSegment StartX=100 StartY=1 StartZ=0 EndX=89.6 EndY=1 EndZ=0
    g7: LineSegment StartX=89.6 StartY=1 StartZ=0 EndX=89.6 EndY=0 EndZ=0
  constraints (25):
    c: Coincident(g0,g1)
    c: Coincident(g1,g2)
    c: Coincident(g2,g3)
    c: Coincident(g3,g0)
    c: Horizontal(g0)
    c: Horizontal(g2)
    c: Vertical(g1)
    c: Vertical(g3)
    c: PointOnObject(g0,g-1)
    c: DistanceX(g0) = 48.5
    c: Distance(g3) = 4
    c: DistanceX(g1) = 86.4
    c: Coincident(g4,g5)
    c: Coincident(g5,g6)
    c: Coincident(g6,g7)
    c: Coincident(g7,g4)
    c: Horizontal(g4)
    c: Horizontal(g6)
    c: Vertical(g5)
    c: Vertical(g7)
    c: PointOnObject(g4,g-1)
    c: Distance(g1,g7) = 3.2
    c: DistanceX(g4) = 100
    c: DistanceY(g6) = 1
    c: DistanceX(g4) = 89.6
FEATURE [PartDesign::Pocket] Pocket
  BaseFeature = -> Pad
  Length = 5
  Length2 = 100
  Profile = -> Sketch001
  Refine = true
  Type = 1
FEATURE [PartDesign::Fillet] Fillet
  Base = -> Pocket [Edge17,Edge36]
  BaseFeature = -> Pocket
  Radius = 1
  Refine = true
  SupportTransform = false
FEATURE [PartDesign::Fillet] Fillet002
  Base = -> Fillet [Edge40,Edge36]
  BaseFeature = -> Fillet
  Radius = 2
  Refine = true
  SupportTransform = false
FEATURE [PartDesign::Fillet] Fillet003
  Base = -> Fillet002 [Edge26]
  BaseFeature = -> Fillet002
  Radius = 0.99
  Refine = true
  SupportTransform = false
FEATURE [Sketcher::SketchObject] Sketch002
  FullyConstrained = true
  MapMode = 5
  Support = -> [XY_Plane001]
  sketch-geometry (2):
    g0: Circle CenterX=88 CenterY=1.4 CenterZ=0 NormalX=0 NormalY=0 NormalZ=1 AngleXU=0 Radius=1
    g1: Circle CenterX=88 CenterY=8 CenterZ=0 NormalX=0 NormalY=0 NormalZ=1 AngleXU=0 Radius=1
  constraints (6):
    c: Vertical(g0,g1)
    c: Distance(g1,g0) = 6.6
    c: Radius(g0) = 1
    c: Radius(g1) = 1
    c: DistanceX(g0) = 88
    c: DistanceY(g0) = 1.4
FEATURE [PartDesign::Hole] Hole
  BaseFeature = -> Fillet003
  Depth = 25
  DepthType = 0
  Diameter = 1.2
  DrillForDepth = false
  DrillPoint = 1
  DrillPointAngle = 118
  HoleCutCountersinkAngle = 90
  HoleCutCustomValues = false
  HoleCutDepth = 0
  HoleCutDiameter = 6.1
  HoleCutType = 0
  ModelActualThread = false
  Profile = -> Sketch002
  Refine = true
  Tapered = false
  TaperedAngle = 90
  ThreadAngle = 0
  ThreadClass = 0
  ThreadCutOffInner = 0
  ThreadCutOffOuter = 0
  ThreadDirection = 0
  ThreadFit = 0
  ThreadPitch = 0
  ThreadSize = 0
  ThreadType = 0
  Threaded = false
FEATURE [PartDesign::Body] Body
  Group = -> [Sketch,Pad,Sketch001,Pocket,Fillet,Fillet002,Fillet003,Sketch002,Hole]
  Origin = -> Origin001
  Tip = -> Hole
FEATURE [App::Part] PCB_Board
  Group = -> [LCS_0,Body]
  Origin = -> Origin
